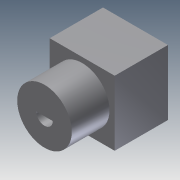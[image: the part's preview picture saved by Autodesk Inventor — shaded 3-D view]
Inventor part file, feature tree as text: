
AUTODESK INVENTOR PART (.ipt)
format: ipt  version: 2011 (Build 150239000, 239)  size: 105,472 bytes
history: native  units: in
note: dims shown in document units (in); Inventor stores cm internally (conversion verified against a paired STEP export)
features: extrude x7, sketch x7
ambient origin geometry x8: Origin, YZ Plane, XZ Plane, XY Plane, X Axis, Y Axis, Z Axis, Center Point
bodies: Solid1 (feature_tree)
feature tree (14):
  extrude  "Extrusion1"  Depth=1.9685in
  extrude  "Extrusion2"  Depth=1.6535in
  extrude  "Extrusion3"  Depth=0.5in
  extrude  "Extrusion4"  Depth=0.8268in TaperAngle=0.0deg
  extrude  "Extrusion5"  Depth=0.315in TaperAngle=0.0deg
  extrude  "Extrusion6"  [1 undecoded]
  extrude  "Extrusion7"  [1 undecoded]
  sketch  "Sketch1"  dims[d0=1.9685in d1=1.9685in]
  sketch  "Sketch2"  dims[d2=1.6142in d3=0.0in d4=1.6535in]
  sketch  "Sketch3"  dims[d5=1.1417in d6=0.0in d7=0.5in]
  sketch  "Sketch4"  dims[d8=1.1417in d9=0.0in d10=0.8268in d11=0.0in]
  sketch  "Sketch5"  dims[d12=0.0394in d13=0.0in d14=0.315in d15=0.0in]
  sketch  "Sketch6"  dims[d16=0.0394in d17=0.0in]
  sketch  "Sketch7"
note: 2 required parameter values undecoded (feature->parameter linkage not recoverable at this tier; creation-order binding heuristic only, values carry confidence <= 0.55)
